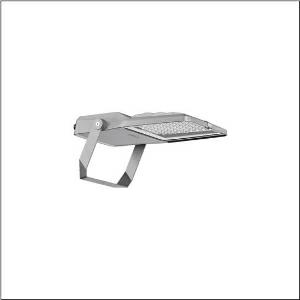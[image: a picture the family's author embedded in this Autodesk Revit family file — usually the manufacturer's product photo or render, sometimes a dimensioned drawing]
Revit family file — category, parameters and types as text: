
# Revit family: floodlight_fl_21_mini___pl43_5xa7772c5a1a_8449
name_source: partatom
category: Lighting Fixtures
units: mm (PartAtom-declared; Revit-internal decimal feet)

## family parameters
Cut with Voids When Loaded = No
Host = Face
Light Source = No
Part Type = Normal
Room Calculation Point = No
Round Connector Dimension = Use Diameter
Shared = No

## types (1)
- --- (1 x LED, 11690 lm, 87.2 W, 4000K)
    Apparent Load = 87 VA
    CIE Flux Codes = 27 78 99 100 100
    Color Rendering = 80
    Color Temperature = 4000K
    Default Elevation = 1800 mm
    Description = Floodlight FL 21 mini, floodlight, primary light control with lens, of PMMA, primary optical cover: protective disc, of toughened safety glass, transparent, light distribution: PL43, light emission: direct distribution, installation type: surface-mounted, LED, High Power LED, rated luminous flux: 11.690lm, luminous efficacy: 134lm/W, light colour: 840, colour temperature: 4000K, control gear: ECG iQ, control: Street-Remote, Auto-Match, Temp-Guard, Night-Set, Smart-Wire, Desk-Remote (wireless, voltage-free reading and setting of iQ features in the workshop via application-optimized NFC function/RFID function), optimised constant luminous flux control (CLO 2.0), with terminal, 6-pole, mains connection: 220..240V, AC, 50/60Hz, start of lifetime: 87W, end of lifetime: 92W, reduction: 40W, luminaire housing, of diecast aluminium, powder-coated, Siteco® metallic grey (DB 702S), corrosivity category C5 according to DIN EN ISO 12944, mounting bracket, of steel, galvanised, powder-coated, Siteco® metallic grey (DB 702S), protection rating (complete): IP66, insulation class (complete): insulation class II (safety insulation), certification: CE, ENEC, VDE, protection symbol: D, impact resistance: IK08, permissible operating ambient temperature: -40..+40°C, permissible operating ambient temperature for outdoor applications: -40..+50°C, standard: DIN EN 12944, packaging unit: 1 piece

Light Distribution: PL43
    Height = 70 mm
    Lamp = 1 x LED
    Lamp Light Flux = 11690 lm
    Lamp Power = 87.2 W
    Lamp count = 1
    Length = 485 mm
    Luminous efficacy = 134 lm/W
    Manufacturer = Siteco
    ModVariant = No
    Model = 5XA7772C5A1A
    Number of Poles = 1
    OnlyDefault = Yes
    Power Factor = 1
    Product Name = Floodlight FL 21 mini | PL43
    Product group = floodlight | pylon top
    ProductGroupID = 6101
    Protection Class = Protection class II
    Protection Degree = IP 66
    RLX_Detail_Level = 1
    RlxData = <blob elided: 96157 chars, md5=e535c2ea>
    Socket = socket
    Standby Power = 0 W
    System Light Flux = 11690 lm
    System Power = 87 W
    Type Comments = factory setting: luminous flux: 100 % | dim-lin: 254 | 456 mA
    Type Image = l_1006845.jpg
    URL = http://relux.com
    VarID = @adj_073313
    Voltage = 0 V
    Weight = 0.00 kg
    Width = 337 mm

## geometry (parser evidence)
native form markers: Blend x4, Sweep x11
no freeform markers — native parametric forms only
